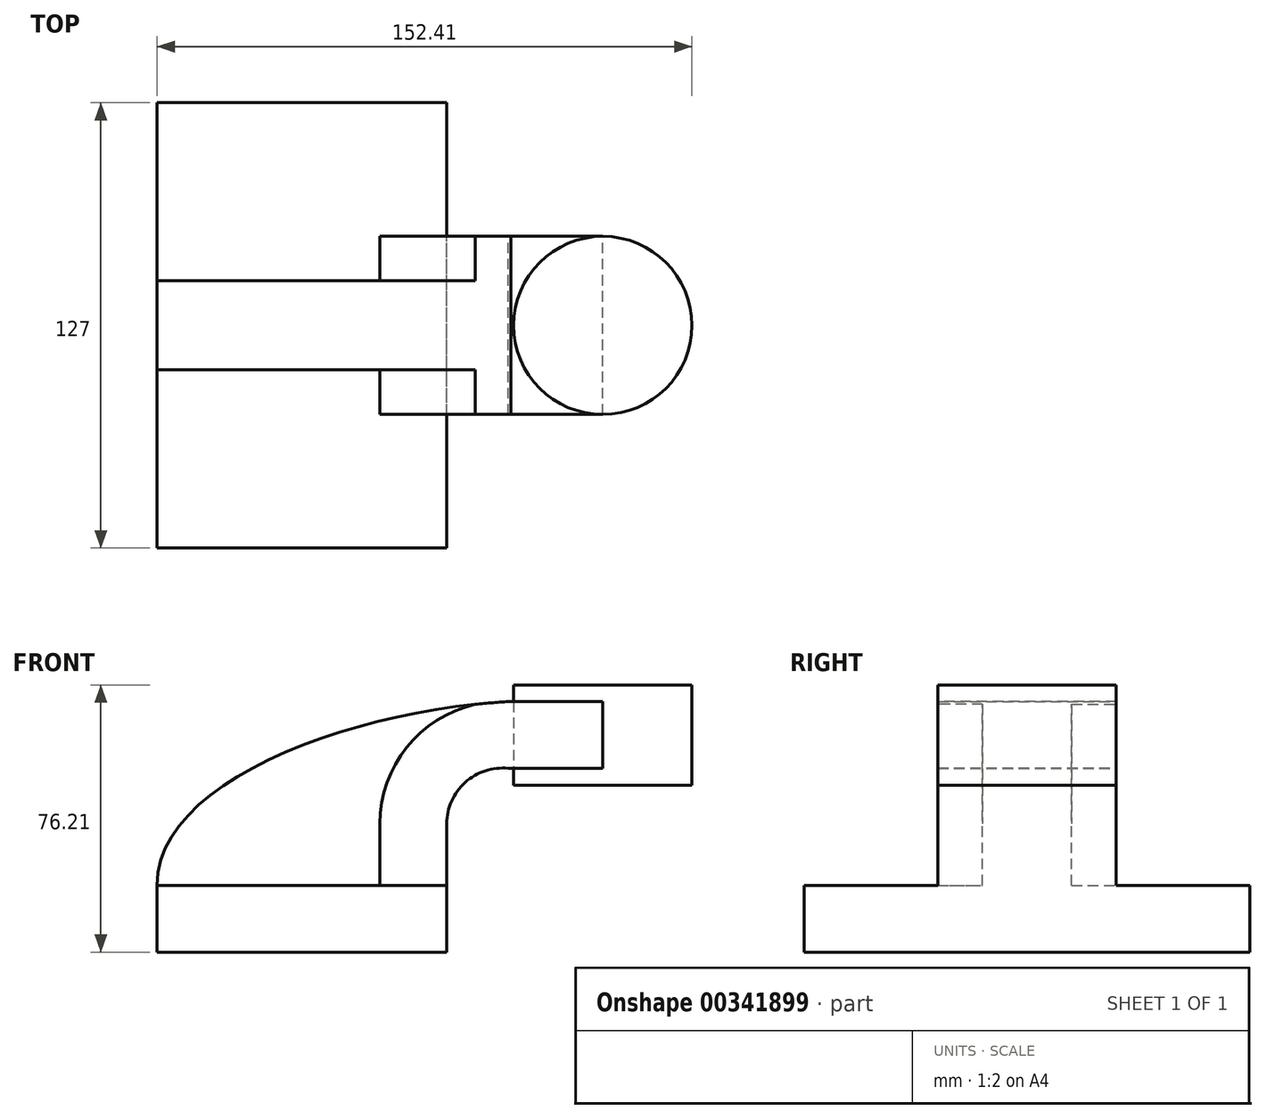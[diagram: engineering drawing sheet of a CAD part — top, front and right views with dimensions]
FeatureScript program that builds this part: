
annotation { "Feature Type Name" : "Feature", "Feature Type Description" : "" }
export const myFeature = defineFeature(function(context is Context, id is Id, definition is map)
    precondition{}
    {
        {
            var Q0;
            Q0=qCreatedBy(makeId("Front.planeOp"),FACE);
            var sketch = newSketch(context, id + "F0", { "sketchPlane" : qUnion([Q0])});
            skLineSegment(sketch, "E0.bottom", {"start": v(41.27, 9.53) * mm, "end": v(-41.28, 9.53) * mm});
            skLineSegment(sketch, "E0.top", {"start": v(41.28, -9.52) * mm, "end": v(-41.27, -9.52) * mm});
            skLineSegment(sketch, "E0.left", {"start": v(41.28, 9.53) * mm, "end": v(41.28, -9.52) * mm});
            skLineSegment(sketch, "E0.right", {"start": v(-41.28, 9.53) * mm, "end": v(-41.27, -9.52) * mm});
            skPoint(sketch, "E0.middle", {"position": v(0, 0) * mm});
            skLineSegment(sketch, "E1.bottom", {"start": v(60.33, 66.68) * mm, "end": v(111.12, 66.68) * mm});
            skLineSegment(sketch, "E1.top", {"start": v(60.33, 38.1) * mm, "end": v(111.12, 38.1) * mm});
            skLineSegment(sketch, "E1.left", {"start": v(60.33, 66.68) * mm, "end": v(60.33, 38.1) * mm});
            skLineSegment(sketch, "E1.right", {"start": v(111.13, 66.68) * mm, "end": v(111.12, 38.1) * mm});
            skLineSegment(sketch, "E2", {"start": v(41.27, 9.53) * mm, "end": v(41.27, 27.08) * mm});
            skArc(sketch, "E3", {"start": v(41.27, 27.08) * mm, "mid": v(46.5, 38.85) * mm, "end": v(58.73, 42.88) * mm});
            skLineSegment(sketch, "E4", {"start": v(58.73, 42.88) * mm, "end": v(85.73, 42.88) * mm});
            skPoint(sketch, "E5.endSnap0", {"position": v(85.73, 66.68) * mm});
            skPoint(sketch, "E5.endSnap1", {"position": v(60.33, 52.39) * mm});
            skPoint(sketch, "E6", {"position": v(85.73, 52.39) * mm});
            skLineSegment(sketch, "E7.0", {"start": v(59.5, 61.93) * mm, "end": v(85.73, 61.93) * mm});
            skArc(sketch, "E7.1", {"start": v(22.23, 27.08) * mm, "mid": v(33.3, 52.6) * mm, "end": v(59.5, 61.93) * mm});
            skLineSegment(sketch, "E7.2", {"start": v(22.22, 9.53) * mm, "end": v(22.22, 27.08) * mm});
            skFitSpline(sketch, "E8", {"points": [v(-41.28, 9.52) * mm, v(59.5, 61.93) * mm], "startDerivative": vector(-0.74, 90.35) * mm, "endDerivative": vector(132.7, 6.65) * mm});
            skLineSegment(sketch, "E9", {"start": v(85.73, 38.1) * mm, "end": v(85.73, 66.68) * mm});
            skSolve(sketch);
        }
        {
            var Q0;
            Q0=makeQuery(id+"F0.imprint","IMPRINT",FACE,{"disambiguationData":[TD([[makeQuery(id+"F0.imprint","IMPRINT",EDGE,{"derivedFrom":sQuery(id+"F0.wireOp",EDGE,"E0.top")}),-1.0]])]});
            extrude(context, id + "F1", {"entities" : qUnion([Q0]), "endBound" : BoundingType.SYMMETRIC, "depth" : 127 * mm});
        }
        {
            var Q0;
            {var subQ1=sQuery(id+"F0.wireOp",EDGE,"E2");Q0=makeQuery(id+"F0.imprint","IMPRINT",FACE,{"disambiguationData":[TD([[makeQuery(id+"F0.imprint","IMPRINT",EDGE,{"derivedFrom":subQ1}),1.0]])]});}
            var Q1;
            {var subQ0=sQuery(id+"F0.wireOp",EDGE,"E7.0");var subQ1=sQuery(id+"F0.wireOp",EDGE,"E1.left");var subQ2=makeQuery(id+"F0.imprint","INTERSECT",VERTEX,{"derivedFrom":[subQ1,subQ0]});Q1=makeQuery(id+"F0.imprint","IMPRINT",FACE,{"disambiguationData":[TD([[makeQuery(id+"F0.imprint","IMPRINT",EDGE,{"disambiguationData":[TD([[subQ2,-1.0]])],"derivedFrom":subQ1}),1.0]])]});}
            extrude(context, id + "F2", {"entities" : qUnion([Q0, Q1]), "operationType" : NewBodyOperationType.ADD, "endBound" : BoundingType.SYMMETRIC, "depth" : 50.8 * mm});
        }
        {
            var Q0;
            {var subQ4=sQuery(id+"F0.wireOp",EDGE,"E1.right");Q0=makeQuery(id+"F0.imprint","IMPRINT",FACE,{"disambiguationData":[TD([[makeQuery(id+"F0.imprint","IMPRINT",EDGE,{"derivedFrom":subQ4}),-1.0]])]});}
            var Q1;
            Q1=sQuery(id+"F0.wireOp",EDGE,"E9");
            revolve(context, id + "F3", {"entities" : qUnion([Q0]), "axis" : qUnion([Q1]), "revolveType" : RevolveType.FULL});
        }
        {
            var Q0;
            {var subQ3=sQuery(id+"F0.wireOp",EDGE,"E7.2");Q0=makeQuery(id+"F0.imprint","IMPRINT",FACE,{"disambiguationData":[TD([[makeQuery(id+"F0.imprint","IMPRINT",EDGE,{"derivedFrom":subQ3}),1.0]])]});}
            extrude(context, id + "F4", {"entities" : qUnion([Q0]), "operationType" : NewBodyOperationType.ADD, "endBound" : BoundingType.SYMMETRIC, "depth" : 25.4 * mm});
        }
    });
